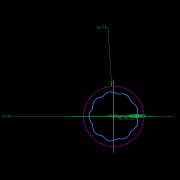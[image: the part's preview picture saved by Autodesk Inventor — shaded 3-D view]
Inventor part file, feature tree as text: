
AUTODESK INVENTOR PART (.ipt)
format: ipt  version: 2022.2 (Build 262287010, 287A)  size: 536,064 bytes
history: native  units: mm
features: other x19, extrude x19, sketch x12, pattern_circular x9, plane x3, fillet x2, move_body x2, revolve x2, draft x2, chamfer x2
ambient origin geometry x8: Origin, YZ Plane, XZ Plane, XY Plane, X Axis, Y Axis, Z Axis, Center Point
bodies: Solid5 (feature_tree)
feature tree (72):
  other  "CrossSection1"
  sketch  "Sketch7"  dims[d90=61.984365mm]
  other  "Roller1"
  other  "Roller2"
  sketch  "Sketch22"  dims[d167=8.972256mm]
  sketch  "Sketch2"  dims[d57=4.025mm]
  sketch  "Sketch23"  dims[d173=10.814812mm]
  other  "RevRoller1"
  fillet  "Fillet1"  Radius=59.246882mm
  pattern_circular  "Circular Pattern13"  Count=360  [1 undecoded]
  move_body  "Move Body7"
  revolve  "Revolution13"  [1 undecoded]
  fillet  "Fillet3"  Radius=0.025mm
  pattern_circular  "Circular Pattern14"  [2 undecoded]
  move_body  "Move Body6"
  revolve  "Revolution14"  [1 undecoded]
  other  "OuterRim_Top2"
  other  "OuterRim_Bottom2"
  plane  "Work Plane7"
  sketch  "Sketch47"  dims[d349=47.575591mm]
  sketch  "Sketch48"  dims[d350=47.575427mm]
  extrude  "Extrusion39"  Depth=0.5mm
  extrude  "Extrusion40"  Depth=0.5mm
  pattern_circular  "Circular Pattern28"  Angle=360.0deg  [1 undecoded]
  sketch  "Sketch49"  dims[d351=0.025mm d352=0.025mm d354=0.1mm d355=16.1595mm d356=16.159664mm d358=360.0deg d359=0.5mm d360=240.0mm d361=360.0deg d363=1.308997mm d367=8.1mm d370=0.1mm d371=1.0mm d372=1.308997mm d373=90.0deg d374=0.5mm d375=240.0mm d376=360.0deg d378=90.0deg d379=0.1mm d380=0.1mm d381=0.1mm d382=0.1mm d383=0.1mm d384=11.193516mm d385=0.0mm d386=0.0mm d391=50.0mm d392=75.0mm d393=1.5mm d394=1.5mm d395=1.5mm d396=1.5mm d397=90.0deg d398=90.0deg d399=90.0deg d400=75.0mm d401=11.193516mm d402=0.0mm d486=0.436332mm d487=0.5mm d488=2.0mm d489=0.0mm d490=20.0mm d495=2.5mm d496=8.0mm d506=13.856406mm d507=55.5mm d508=8.0mm d509=0.05mm d510=2.5mm d511=30.0deg d512=12.0mm d513=6.0mm d514=0.2mm d515=30.0deg d516=131.0mm d517=65.5mm d518=0.2mm d519=100.0mm d520=120.0mm d521=2.0mm d522=150.0mm d530=50.0mm d531=5.5mm d532=5.5mm d533=5.5mm d534=85.75mm d535=73.5mm d536=61.25mm d537=24.5mm d538=3.0mm d539=2.4mm d540=0.0mm d541=0.0mm d542=0.0mm d543=5.5mm d544=3.0mm d545=0.0mm d546=90.0mm d547=360.0deg d549=3.0mm d550=3.0mm d551=2.4mm d552=0.0mm d553=5.596758mm d554=0.0mm d555=2.4mm d556=0.0mm d557=5.596758mm d558=0.0mm d559=5.596758mm d560=0.0mm d561=90.0mm d562=360.0deg d564=60.0mm d565=360.0deg d567=5.5mm d568=5.5mm d569=3.0mm d570=0.0mm d571=5.596758mm d572=0.0mm d573=3.0mm d574=0.0mm d575=5.596758mm d576=0.0mm d577=90.0mm d578=360.0deg d580=60.0mm d581=360.0deg d584=20.0mm d585=8.0mm d587=1.75mm d589=3.0mm d592=2.0mm d593=12.0mm d594=12.0mm d600=0.5mm d601=2.0mm d602=45.0deg d603=0.5mm d604=2.0mm d605=45.0deg d606=0.436332mm d607=0.5mm d608=0.0mm d609=20.0mm d611=360.0deg d613=0.0mm d614=0.0mm d617=0.99971mm d618=100.0mm d620=69.0mm d621=3.0mm d622=5.5mm d623=5.596758mm d624=0.0mm d625=3.0mm d626=0.0mm d627=60.0mm d628=360.0deg d630=5.5mm d631=3.0mm d632=5.596758mm d633=0.0mm d634=2.593516mm d635=0.0mm d636=60.0mm d637=360.0deg d16=0.872665mm d17=0.872665mm d49=0.872665mm d50=0.872665mm d51=0.872665mm d52=0.872665mm d236=0.5mm d237=0.872665mm d238=0.5mm d239=0.872665mm d282=1.0mm d283=1.0mm d284=1.0mm d285=0.15mm d286=0.25mm d287=0.375mm d288=14.3117mm d289=0.75mm d290=20.594885mm d291=0.0625mm d292=0.75mm d293=0.375mm d405=0.5mm d406=0.872665mm d407=0.5mm d408=0.872665mm d413=0.5mm d414=0.872665mm d415=0.5mm d416=0.872665mm d417=0.5mm d418=0.872665mm d419=0.5mm d420=0.872665mm d421=0.872665mm d431=0.5mm d432=0.872665mm d433=0.5mm d434=0.872665mm d471=0.5mm d472=0.872665mm d473=0.5mm d474=0.872665mm d497=0.5mm d498=0.872665mm d499=0.5mm d500=0.872665mm d590=0.5mm d591=0.872665mm]
  extrude  "Extrusion41"  Depth=0.5mm
  extrude  "Extrusion42"  Depth=0.5mm
  pattern_circular  "Circular Pattern29"  Angle=360.0deg  [1 undecoded]
  extrude  "Rotor_Ring"  Depth=0.5mm
  draft  "FaceDraft2"
  sketch  "Sketch30"  dims[d201=75.0mm d232=0.0mm d233=3600.0mm]
  plane  "Work Plane5"
  other  "Rotor Featurs"
  other  "RotorRim_Bottom"
  extrude  "Extrusion24"  Depth=0.5mm
  extrude  "Extrusion25"  Depth=0.5mm
  extrude  "Extrusion26"  Depth=0.5mm
  pattern_circular  "Circular Pattern23"  [2 undecoded]
  sketch  "Sketch41"  dims[d346=0.025mm]
  extrude  "Extrusion27"  TaperAngle=90.0deg  [1 undecoded]
  extrude  "Extrusion28"  Depth=0.5mm
  pattern_circular  "Circular Pattern24"  Count=24  [1 undecoded]
  extrude  "Extrusion29"  TaperAngle=360.0deg  [1 undecoded]
  extrude  "Extrusion30"  TaperAngle=90.0deg  [1 undecoded]
  extrude  "Extrusion31"  Depth=0.5mm
  pattern_circular  "Circular Pattern25"  [2 undecoded]
  sketch  "Sketch42"  dims[d347=0.1mm]
  extrude  "Extrusion32"  Depth=0.5mm
  extrude  "Extrusion33"  Depth=0.5mm
  extrude  "Extrusion34"  Depth=0.5mm
  extrude  "Extrusion35"  Depth=0.5mm
  pattern_circular  "Circular Pattern26"  [2 undecoded]
  pattern_circular  "Circular Pattern27"  [2 undecoded]
  chamfer  "Chamfer1"  Distance=50.0mm
  chamfer  "Chamfer2"  Distance=75.0mm
  draft  "FaceDraft4"
  plane  "Work Plane6"
  sketch  "Sketch43"  dims[d348=0.1mm]
  extrude  "Extrusion37"  Depth=0.5mm
  extrude  "Extrusion38"  Depth=0.5mm
  other  "2D Equation Curve1"
  sketch  "Sketch40"  dims[d343=16.1595mm d344=16.159664mm d345=0.025mm]
  other  "Work Axis6"
  other  "Work Axis7"
  other  "Work Axis8"
  other  "Work Axis9"
  other  "Work Axis10"
  other  "Work Point1"
  other  "Work Point2"
  other  "Work Point3"
  other  "Work Point4"
  other  "Work Point5"
note: 19 required parameter values undecoded (feature->parameter linkage not recoverable at this tier; creation-order binding heuristic only, values carry confidence <= 0.55)